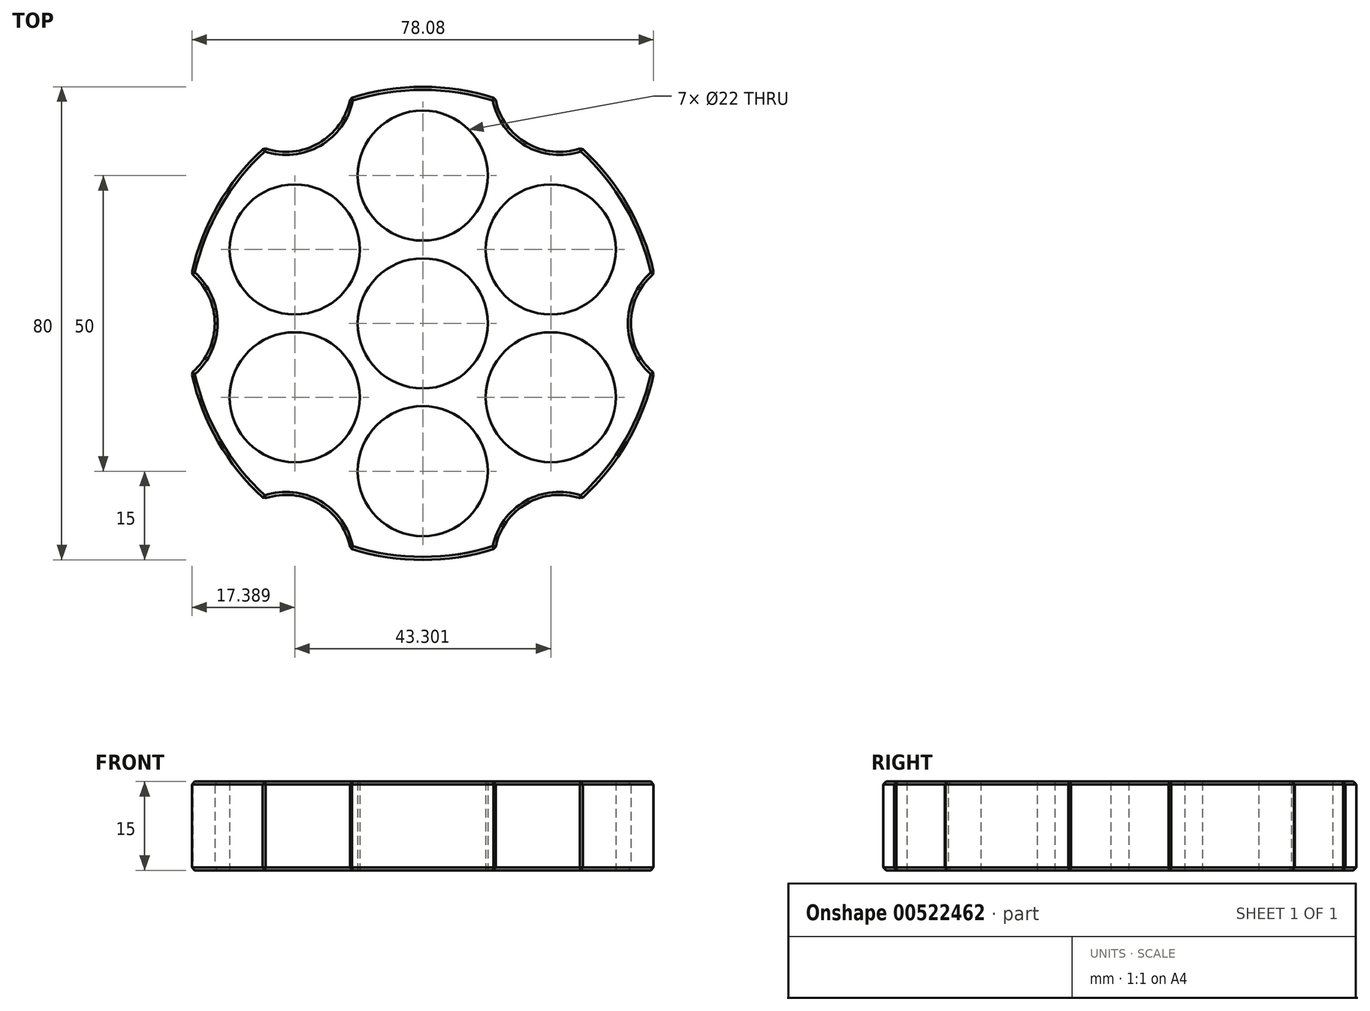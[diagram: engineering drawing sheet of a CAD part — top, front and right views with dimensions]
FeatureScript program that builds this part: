
annotation { "Feature Type Name" : "Feature", "Feature Type Description" : "" }
export const myFeature = defineFeature(function(context is Context, id is Id, definition is map)
    precondition{}
    {
        {
            var Q0;
            Q0=qCreatedBy(makeId("Top.planeOp"),FACE);
            var sketch = newSketch(context, id + "F0", { "sketchPlane" : qUnion([Q0])});
            skCircle(sketch, "E0.cCircle", {"center": v(0, 0) * mm, "radius": 40 * mm, "construction": true});
            skPoint(sketch, "E0.0.midPoint", {"position": v(0, -40) * mm});
            skArc(sketch, "E1", {"start": v(-26.84, 29.66) * mm, "mid": v(-17.6, 30.47) * mm, "end": v(-12.26, 38.07) * mm});
            skArc(sketch, "E2", {"start": v(12.26, 38.07) * mm, "mid": v(17.6, 30.47) * mm, "end": v(26.84, 29.66) * mm});
            skArc(sketch, "E3", {"start": v(39.1, 8.42) * mm, "mid": v(35.19, 0) * mm, "end": v(39.1, -8.42) * mm});
            skArc(sketch, "E4", {"start": v(26.84, -29.66) * mm, "mid": v(17.6, -30.47) * mm, "end": v(12.26, -38.07) * mm});
            skArc(sketch, "E5", {"start": v(-12.26, -38.07) * mm, "mid": v(-17.6, -30.47) * mm, "end": v(-26.84, -29.66) * mm});
            skArc(sketch, "E6", {"start": v(-39.1, -8.42) * mm, "mid": v(-35.19, 0) * mm, "end": v(-39.1, 8.42) * mm});
            skPoint(sketch, "E7", {"position": v(34.64, 20) * mm});
            skPoint(sketch, "E8", {"position": v(-34.64, 20) * mm});
            skLineSegment(sketch, "E9", {"start": v(34.64, 20) * mm, "end": v(-34.64, -20) * mm, "construction": true});
            skLineSegment(sketch, "E10", {"start": v(-34.64, 20) * mm, "end": v(34.64, -20) * mm, "construction": true});
            skLineSegment(sketch, "E11", {"start": v(0, 40) * mm, "end": v(0, -40) * mm, "construction": true});
            skCircle(sketch, "E12", {"center": v(0, 0) * mm, "radius": 11 * mm});
            skPoint(sketch, "E13", {"position": v(-21.65, 12.5) * mm});
            skCircle(sketch, "E14", {"center": v(-21.65, 12.5) * mm, "radius": 11 * mm});
            skPoint(sketch, "E15", {"position": v(0, 25) * mm});
            skPoint(sketch, "E16", {"position": v(21.65, 12.5) * mm});
            skPoint(sketch, "E17", {"position": v(21.65, -12.5) * mm});
            skPoint(sketch, "E18", {"position": v(0, -25) * mm});
            skPoint(sketch, "E19", {"position": v(-21.65, -12.5) * mm});
            skCircle(sketch, "E20", {"center": v(-21.65, -12.5) * mm, "radius": 11 * mm});
            skCircle(sketch, "E21", {"center": v(0, 25) * mm, "radius": 11 * mm});
            skCircle(sketch, "E22", {"center": v(21.65, 12.5) * mm, "radius": 11 * mm});
            skCircle(sketch, "E23", {"center": v(21.65, -12.5) * mm, "radius": 11 * mm});
            skCircle(sketch, "E24", {"center": v(0, -25) * mm, "radius": 11 * mm});
            skArc(sketch, "E25", {"start": v(-26.84, 29.66) * mm, "mid": v(-34.64, 20) * mm, "end": v(-39.1, 8.42) * mm});
            skArc(sketch, "E26.trimOffspring", {"start": v(12.26, 38.07) * mm, "mid": v(0, 40) * mm, "end": v(-12.26, 38.07) * mm});
            skArc(sketch, "E27.trimOffspring", {"start": v(39.1, 8.42) * mm, "mid": v(34.64, 20) * mm, "end": v(26.84, 29.66) * mm});
            skArc(sketch, "E28.trimOffspring", {"start": v(-39.1, -8.42) * mm, "mid": v(-34.64, -20) * mm, "end": v(-26.84, -29.66) * mm});
            skArc(sketch, "E29.trimOffspring", {"start": v(-12.26, -38.07) * mm, "mid": v(0, -40) * mm, "end": v(12.26, -38.07) * mm});
            skArc(sketch, "E30.trimOffspring", {"start": v(26.84, -29.66) * mm, "mid": v(34.64, -20) * mm, "end": v(39.1, -8.42) * mm});
            skSolve(sketch);
        }
        {
            var Q0;
            Q0=makeQuery(id+"F0.imprint","IMPRINT",FACE,{"disambiguationData":[TD([[makeQuery(id+"F0.imprint","IMPRINT",EDGE,{"derivedFrom":sQuery(id+"F0.wireOp",EDGE,"E1")}),-1.0]])]});
            extrude(context, id + "F1", {"entities" : qUnion([Q0]), "depth" : 15 * mm, "offsetDistance" : 25 * mm});
        }
        {
            var Q0;
            Q0=makeQuery(id+"F1.opExtrude","SWEPT_FACE",FACE,{"disambiguationData":[OSD([sQuery(id+"F0.wireOp",EDGE,"E25")])]});
            var Q1;
            Q1=makeQuery(id+"F1.opExtrude","SWEPT_FACE",FACE,{"disambiguationData":[OSD([sQuery(id+"F0.wireOp",EDGE,"E1")])]});
            var Q2;
            Q2=makeQuery(id+"F1.opExtrude","SWEPT_FACE",FACE,{"disambiguationData":[OSD([sQuery(id+"F0.wireOp",EDGE,"E26.trimOffspring")])]});
            var Q3;
            Q3=makeQuery(id+"F1.opExtrude","SWEPT_FACE",FACE,{"disambiguationData":[OSD([sQuery(id+"F0.wireOp",EDGE,"E6")])]});
            var Q4;
            Q4=makeQuery(id+"F1.opExtrude","SWEPT_FACE",FACE,{"disambiguationData":[OSD([sQuery(id+"F0.wireOp",EDGE,"E2")])]});
            var Q5;
            Q5=makeQuery(id+"F1.opExtrude","SWEPT_FACE",FACE,{"disambiguationData":[OSD([sQuery(id+"F0.wireOp",EDGE,"E27.trimOffspring")])]});
            var Q6;
            Q6=makeQuery(id+"F1.opExtrude","SWEPT_FACE",FACE,{"disambiguationData":[OSD([sQuery(id+"F0.wireOp",EDGE,"E3")])]});
            var Q7;
            Q7=makeQuery(id+"F1.opExtrude","SWEPT_FACE",FACE,{"disambiguationData":[OSD([sQuery(id+"F0.wireOp",EDGE,"E30.trimOffspring")])]});
            var Q8;
            Q8=makeQuery(id+"F1.opExtrude","SWEPT_FACE",FACE,{"disambiguationData":[OSD([sQuery(id+"F0.wireOp",EDGE,"E4")])]});
            var Q9;
            Q9=makeQuery(id+"F1.opExtrude","SWEPT_FACE",FACE,{"disambiguationData":[OSD([sQuery(id+"F0.wireOp",EDGE,"E29.trimOffspring")])]});
            var Q10;
            Q10=makeQuery(id+"F1.opExtrude","SWEPT_FACE",FACE,{"disambiguationData":[OSD([sQuery(id+"F0.wireOp",EDGE,"E5")])]});
            var Q11;
            Q11=makeQuery(id+"F1.opExtrude","SWEPT_FACE",FACE,{"disambiguationData":[OSD([sQuery(id+"F0.wireOp",EDGE,"E28.trimOffspring")])]});
            chamfer(context, id + "F2", {"entities" : qUnion([Q0, Q1, Q2, Q3, Q4, Q5, Q6, Q7, Q8, Q9, Q10, Q11]), "width" : 0.5 * mm, "tangentPropagation" : true});
        }
    });
